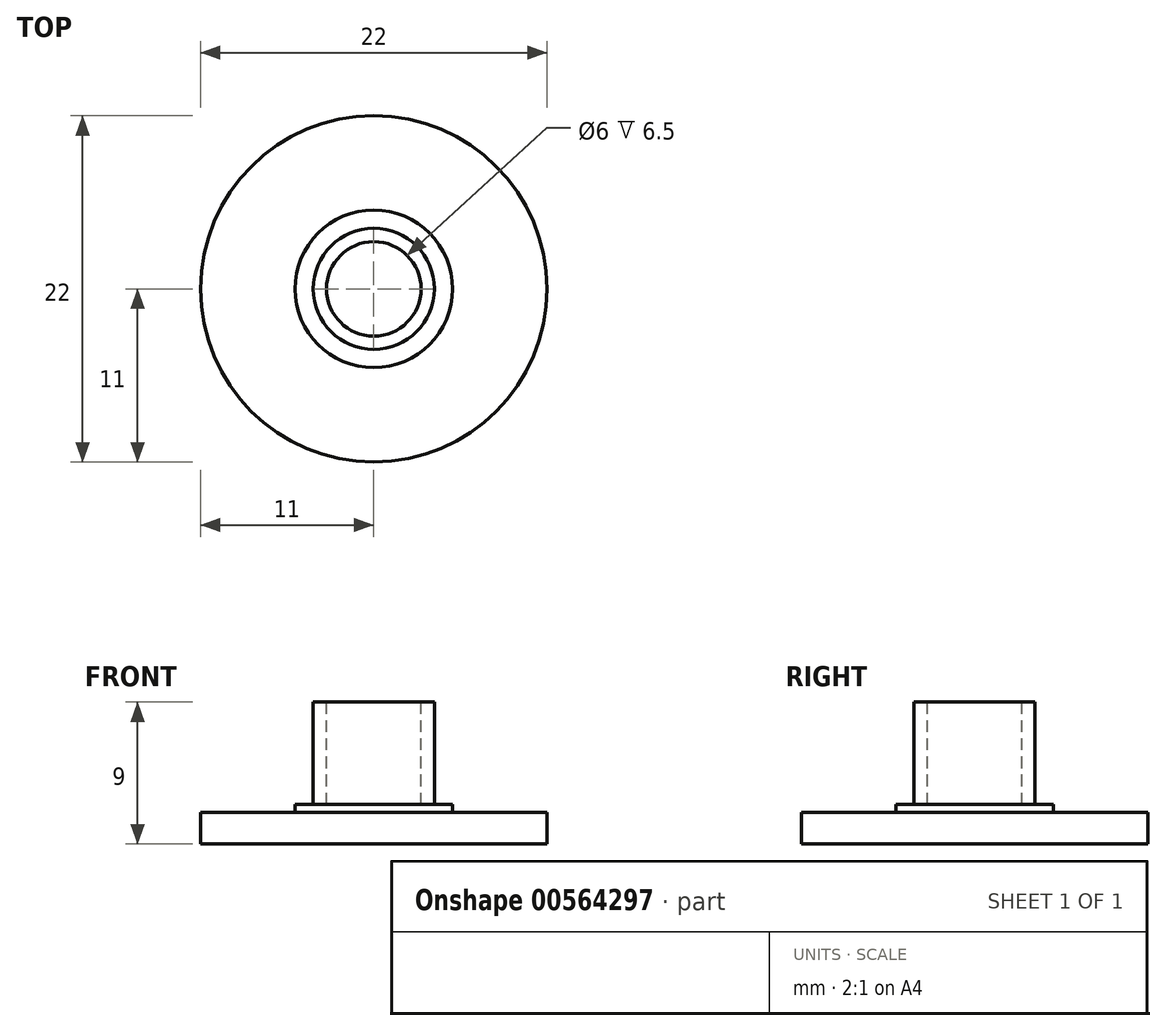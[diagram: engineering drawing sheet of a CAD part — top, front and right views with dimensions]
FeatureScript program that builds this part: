
annotation { "Feature Type Name" : "Feature", "Feature Type Description" : "" }
export const myFeature = defineFeature(function(context is Context, id is Id, definition is map)
    precondition{}
    {
        {
            var Q0;
            Q0=qCreatedBy(makeId("Top.planeOp"),FACE);
            var sketch = newSketch(context, id + "F0", { "sketchPlane" : qUnion([Q0])});
            skCircle(sketch, "E0", {"center": v(0, 0) * mm, "radius": 11 * mm});
            skSolve(sketch);
        }
        {
            var Q0;
            Q0=makeQuery(id+"F0.imprint","IMPRINT",FACE,{"disambiguationData":[TD([[makeQuery(id+"F0.imprint","IMPRINT",EDGE,{"derivedFrom":sQuery(id+"F0.wireOp",EDGE,"E0")}),1.0]])]});
            extrude(context, id + "F1", {"entities" : qUnion([Q0]), "depth" : 2 * mm, "offsetDistance" : 25 * mm});
        }
        {
            var Q0;
            Q0=makeQuery(id+"F1.opExtrude","CAP_FACE",FACE,{"disambiguationData":[OSD([sQuery(id+"F0.wireOp",EDGE,"E0")])],"isStart":false});
            var sketch = newSketch(context, id + "F2", { "sketchPlane" : qUnion([Q0])});
            skCircle(sketch, "E1", {"center": v(0, 0) * mm, "radius": 5 * mm});
            skSolve(sketch);
        }
        {
            var Q0;
            Q0=makeQuery(id+"F2.imprint","IMPRINT",FACE,{"disambiguationData":[TD([[makeQuery(id+"F2.imprint","IMPRINT",EDGE,{"derivedFrom":sQuery(id+"F2.wireOp",EDGE,"E1")}),1.0]])]});
            extrude(context, id + "F3", {"entities" : qUnion([Q0]), "operationType" : NewBodyOperationType.ADD, "depth" : .5 * mm, "offsetDistance" : 25 * mm});
        }
        {
            var Q0;
            Q0=makeQuery(id+"F3.opExtrude","CAP_FACE",FACE,{"disambiguationData":[OSD([sQuery(id+"F2.wireOp",EDGE,"E1")])],"isStart":false});
            var sketch = newSketch(context, id + "F4", { "sketchPlane" : qUnion([Q0])});
            skCircle(sketch, "E2", {"center": v(0, 0) * mm, "radius": 3.85 * mm});
            skSolve(sketch);
        }
        {
            var Q0;
            Q0=makeQuery(id+"F4.imprint","IMPRINT",FACE,{"disambiguationData":[TD([[makeQuery(id+"F4.imprint","IMPRINT",EDGE,{"derivedFrom":sQuery(id+"F4.wireOp",EDGE,"E2")}),1.0]])]});
            extrude(context, id + "F5", {"entities" : qUnion([Q0]), "operationType" : NewBodyOperationType.ADD, "depth" : 6.5 * mm, "offsetDistance" : 25 * mm});
        }
        {
            var Q0;
            Q0=makeQuery(id+"F5.opExtrude","CAP_FACE",FACE,{"disambiguationData":[OSD([sQuery(id+"F4.wireOp",EDGE,"E2")])],"isStart":false});
            var sketch = newSketch(context, id + "F6", { "sketchPlane" : qUnion([Q0])});
            skSolve(sketch);
        }
        {
            var Q0;
            Q0=makeQuery(id+"F6.imprint","IMPRINT",FACE,{"disambiguationData":[TD([[makeQuery(id+"F6.imprint","IMPRINT",EDGE,{"derivedFrom":makeQuery(id+"F5.opExtrude","CAP_EDGE",EDGE,{"disambiguationData":[OSD([sQuery(id+"F4.wireOp",EDGE,"E2")])],"isStart":false})}),1.0]])]});
            var sketch = newSketch(context, id + "F7", { "sketchPlane" : qUnion([Q0])});
            skCircle(sketch, "E3", {"center": v(0, 0) * mm, "radius": 3 * mm});
            skSolve(sketch);
        }
        {
            var Q0;
            Q0=makeQuery(id+"F7.imprint","IMPRINT",FACE,{"disambiguationData":[TD([[makeQuery(id+"F7.imprint","IMPRINT",EDGE,{"derivedFrom":sQuery(id+"F7.wireOp",EDGE,"E3")}),1.0]])]});
            extrude(context, id + "F8", {"entities" : qUnion([Q0]), "operationType" : NewBodyOperationType.REMOVE, "oppositeDirection" : true, "depth" : 6.5 * mm, "offsetDistance" : 25 * mm});
        }
    });
